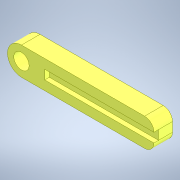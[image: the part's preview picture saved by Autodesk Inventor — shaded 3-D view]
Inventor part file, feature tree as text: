
AUTODESK INVENTOR PART (.ipt)
format: ipt  version: 2020 (Build 240168000, 168)  size: 128,512 bytes
history: native  units: mm
features: extrude x2, sketch x2
ambient origin geometry x8: Origin, YZ Plane, XZ Plane, XY Plane, X Axis, Y Axis, Z Axis, Center Point
bodies: Solid1 (feature_tree)
feature tree (4):
  extrude  "Extrusion1"  Depth=6.0mm
  extrude  "Extrusion2"  Depth=1.0mm
  sketch  "Sketch1"  dims[d0=3.3mm d1=6.0mm]
  sketch  "Sketch2"  dims[d2=2.0mm d3=28.5mm d4=4.0mm d5=0.0mm d6=2.0mm d7=5.0mm d8=1.0mm d9=0.0mm]
